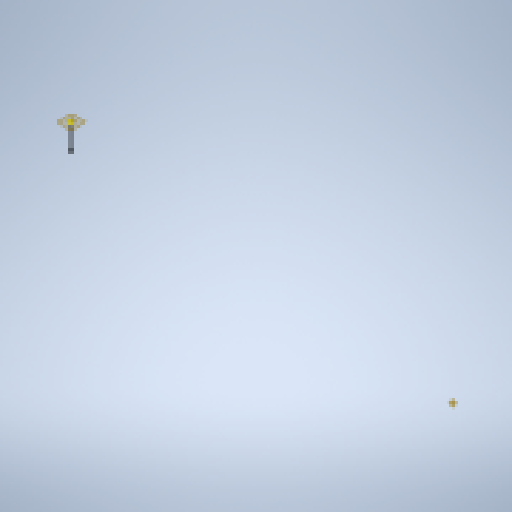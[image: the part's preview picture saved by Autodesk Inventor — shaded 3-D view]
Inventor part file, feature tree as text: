
AUTODESK INVENTOR PART (.ipt)
format: ipt  version: 2025.2 (Build 292293000, 293)  size: 131,072 bytes
history: native  units: in
note: dims shown in document units (in); Inventor stores cm internally (conversion verified against a paired STEP export)
features: other x3, plane x1, sketch x1
ambient origin geometry x8: Origin, YZ Plane, XZ Plane, XY Plane, X Axis, Y Axis, Z Axis, Center Point
feature tree (5):
  other  "Work Point3"
  plane  "Work Plane1"
  sketch  "3D Sketch1"
  other  "Work Point1"
  other  "Work Point2"
